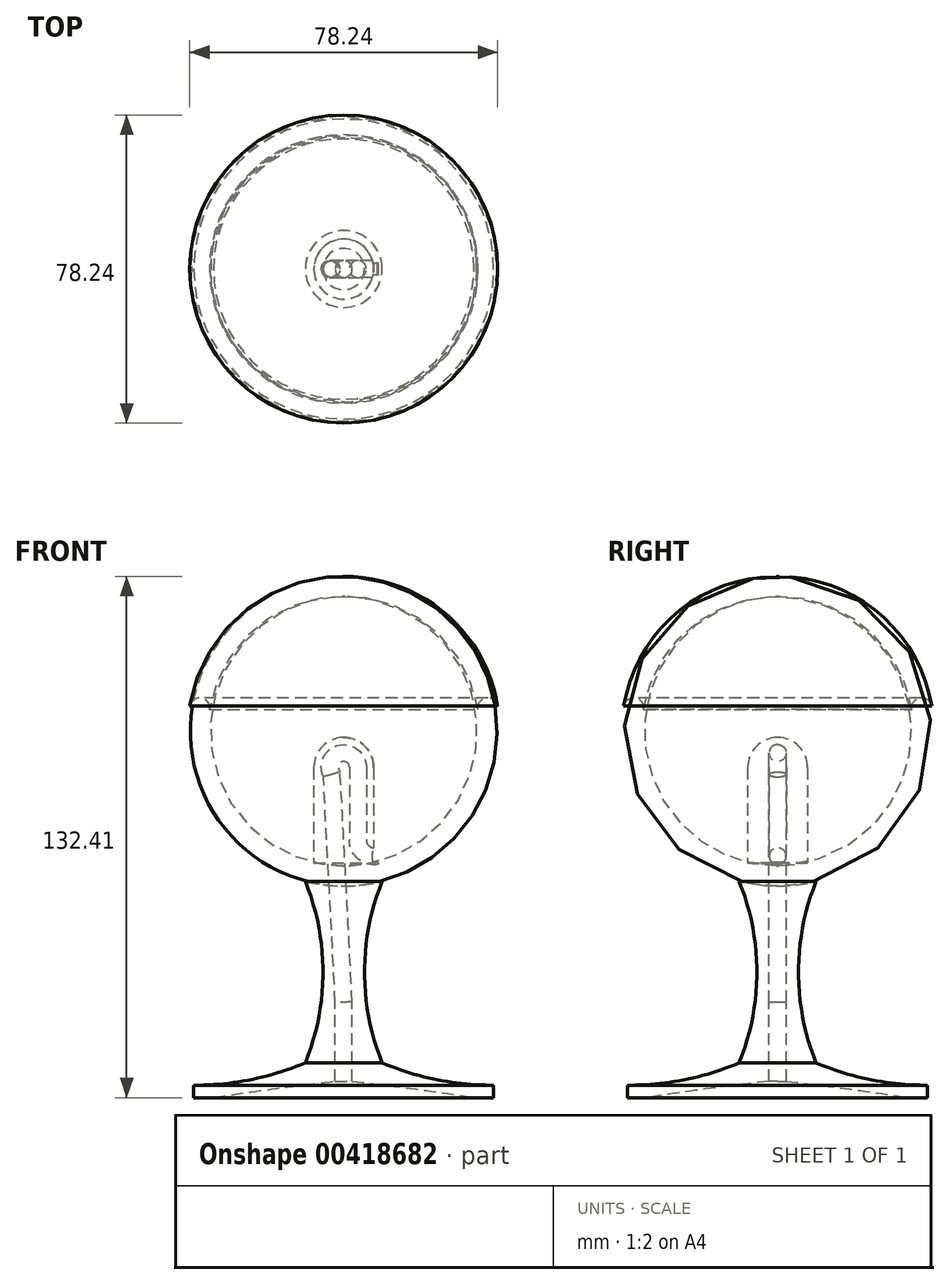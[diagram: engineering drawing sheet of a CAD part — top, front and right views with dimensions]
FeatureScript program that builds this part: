
annotation { "Feature Type Name" : "Feature", "Feature Type Description" : "" }
export const myFeature = defineFeature(function(context is Context, id is Id, definition is map)
    precondition{}
    {
        {
            var Q0;
            Q0=qCreatedBy(makeId("Front.planeOp"),FACE);
            var sketch = newSketch(context, id + "F0", { "sketchPlane" : qUnion([Q0])});
            skLineSegment(sketch, "E0", {"start": v(0, 4.4) * mm, "end": v(0, 91.52) * mm});
            skLineSegment(sketch, "E1", {"start": v(33.49, 101.6) * mm, "end": v(38.71, 101.6) * mm});
            skLineSegment(sketch, "E2", {"start": v(33.07, 0) * mm, "end": v(38.1, 0) * mm});
            skLineSegment(sketch, "E3", {"start": v(38.1, 0) * mm, "end": v(38.1, 3.18) * mm});
            skArc(sketch, "E4", {"start": v(9.77, 54.96) * mm, "mid": v(33.73, 72.39) * mm, "end": v(38.71, 101.6) * mm});
            skArc(sketch, "E5", {"start": v(9.77, 8.87) * mm, "mid": v(23.64, 4.57) * mm, "end": v(38.1, 3.17) * mm});
            skLineSegment(sketch, "E6", {"start": v(7.62, 59.67) * mm, "end": v(7.62, 83.9) * mm});
            skPoint(sketch, "E7.center.orphan", {"position": v(0, 83.9) * mm});
            skArc(sketch, "E8.0", {"start": v(7.62, 59.67) * mm, "mid": v(29.46, 75.14) * mm, "end": v(33.49, 101.6) * mm});
            skArc(sketch, "E9", {"start": v(7.62, 83.9) * mm, "mid": v(5.39, 89.29) * mm, "end": v(0, 91.52) * mm});
            skArc(sketch, "E10", {"start": v(9.77, 54.96) * mm, "mid": v(5.27, 31.91) * mm, "end": v(9.77, 8.87) * mm});
            skArc(sketch, "E11", {"start": v(33.07, 0) * mm, "mid": v(16.56, 2.43) * mm, "end": v(0, 4.4) * mm});
            skSolve(sketch);
        }
        {
            var Q0;
            Q0 = qSketchRegion(id + "F0", true);
            var Q1;
            Q1=sQuery(id+"F0.wireOp",EDGE,"E0");
            revolve(context, id + "F1", {"entities" : qUnion([Q0]), "axis" : qUnion([Q1]), "revolveType" : RevolveType.FULL});
        }
        {
            var Q0;
            Q0=qCreatedBy(makeId("Front.planeOp"),FACE);
            var sketch = newSketch(context, id + "F2", { "sketchPlane" : qUnion([Q0])});
            skArc(sketch, "E12", {"start": v(3.56, 84) * mm, "mid": v(-0.97, 87.43) * mm, "end": v(-3.03, 82.12) * mm});
            skLineSegment(sketch, "E13", {"start": v(3.56, 84) * mm, "end": v(3.56, 65.45) * mm});
            skArc(sketch, "E14", {"start": v(3.56, 65.45) * mm, "mid": v(5.02, 62.3) * mm, "end": v(8.38, 61.36) * mm});
            skLineSegment(sketch, "E15", {"start": v(-3.03, 82.12) * mm, "end": v(0, 24.25) * mm});
            skLineSegment(sketch, "E16", {"start": v(0, 24.25) * mm, "end": v(0, 0) * mm});
            skSolve(sketch);
        }
        {
            var Q0;
            Q0=makeQuery(id+"F1.opRevolve","SWEPT_FACE",FACE,{"disambiguationData":[OSD([sQuery(id+"F0.wireOp",EDGE,"E2")])]});
            var sketch = newSketch(context, id + "F3", { "sketchPlane" : qUnion([Q0])});
            skCircle(sketch, "E17", {"center": v(0, 0) * mm, "radius": 2.16 * mm});
            skSolve(sketch);
        }
        {
            var Q0;
            Q0=makeQuery(id+"F3.imprint","IMPRINT",FACE,{"disambiguationData":[TD([[makeQuery(id+"F3.imprint","IMPRINT",EDGE,{"derivedFrom":sQuery(id+"F3.wireOp",EDGE,"E17")}),1.0]])]});
            var Q1;
            Q1=sQuery(id+"F2.wireOp",EDGE,"E16");
            var Q2;
            Q2=sQuery(id+"F2.wireOp",EDGE,"E15");
            var Q3;
            Q3=sQuery(id+"F2.wireOp",EDGE,"E12");
            var Q4;
            Q4=sQuery(id+"F2.wireOp",EDGE,"E13");
            var Q5;
            Q5=sQuery(id+"F2.wireOp",EDGE,"E14");
            sweep(context, id + "F4", {"operationType" : NewBodyOperationType.REMOVE, "profiles" : qUnion([Q0]), "path" : qUnion([Q1, Q2, Q3, Q4, Q5])});
        }
        {
            var Q0;
            Q0=makeQuery(id+"F1.opRevolve","SWEPT_EDGE",EDGE,{"disambiguationData":[OSD([sQuery(id+"F0.wireOp",EDGE,"E1"),sQuery(id+"F0.wireOp",EDGE,"E8.0")])]});
            var Q1;
            Q1=makeQuery(id+"F1.opRevolve","SWEPT_EDGE",EDGE,{"disambiguationData":[OSD([sQuery(id+"F0.wireOp",EDGE,"E1"),sQuery(id+"F0.wireOp",EDGE,"E4")])]});
            var Q2;
            Q2=makeQuery(id+"FxQKJDNVuqQIBrW_1.opRevolve","SWEPT_EDGE",EDGE,{"disambiguationData":[OSD([sQuery(id+"F0.wireOp",EDGE,"E1"),sQuery(id+"F0.wireOp",EDGE,"E8.0")])]});
            var Q3;
            Q3=makeQuery(id+"FxQKJDNVuqQIBrW_1.opRevolve","SWEPT_EDGE",EDGE,{"disambiguationData":[OSD([sQuery(id+"F0.wireOp",EDGE,"E1"),sQuery(id+"F0.wireOp",EDGE,"E4")])]});
            fillet(context, id + "F5", {"entities" : qUnion([Q0, Q1, Q2, Q3]), "radius" : 2.54 * mm, "tangentPropagation" : true, "allowEdgeOverflow" : false});
        }
    });
